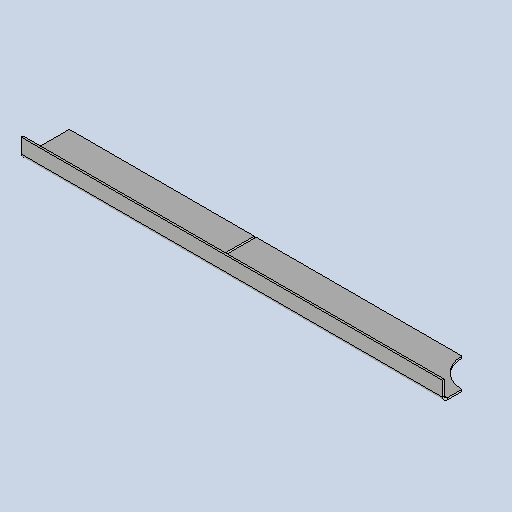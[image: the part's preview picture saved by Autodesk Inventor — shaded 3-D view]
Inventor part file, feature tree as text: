
AUTODESK INVENTOR PART (.ipt)
format: ipt  version: 2025 (Build 290162010, 162A)  size: 266,752 bytes
history: native  units: mm
features: other x5, sketch x5, sheet_metal_op x4, extrude x2
ambient origin geometry x8: Origin, YZ Plane, XZ Plane, XY Plane, X Axis, Y Axis, Z Axis, Center Point
bodies: Solid1 (feature_tree)
feature tree (16):
  sheet_metal_op  "Face1"
  sheet_metal_op  "Flange1"
  extrude  "Extrusion1"  Depth=50.0mm
  other  "Mark1"
  other  "A-Side Definition"
  extrude  "Extrusion3"  Depth=2.0mm
  sketch  "Sketch1"  dims[d0=980.0mm d1=50.0mm]
  other  "Plate1"
  sketch  "Sketch2"  dims[d2=2.0mm d3=2.0mm]
  other  "Plate2"
  sheet_metal_op  "Bend1"
  sheet_metal_op  "Corner1"
  sketch  "Sketch5"  dims[d4=1.0mm]
  sketch  "Sketch7"  dims[d5=4.0mm]
  sketch  "Sketch8"  dims[d6=2.75mm d7=20.0mm d8=90.0deg d9=2.75mm d10=8.0mm d11=2.0mm d12=2.75mm d15=0.0mm d16=0.0mm d30=12.0mm d33=60.0mm d34=2.0mm d35=31.0mm d36=490.0mm d37=0.0mm d38=0.0mm]
  other  "Definition1"
